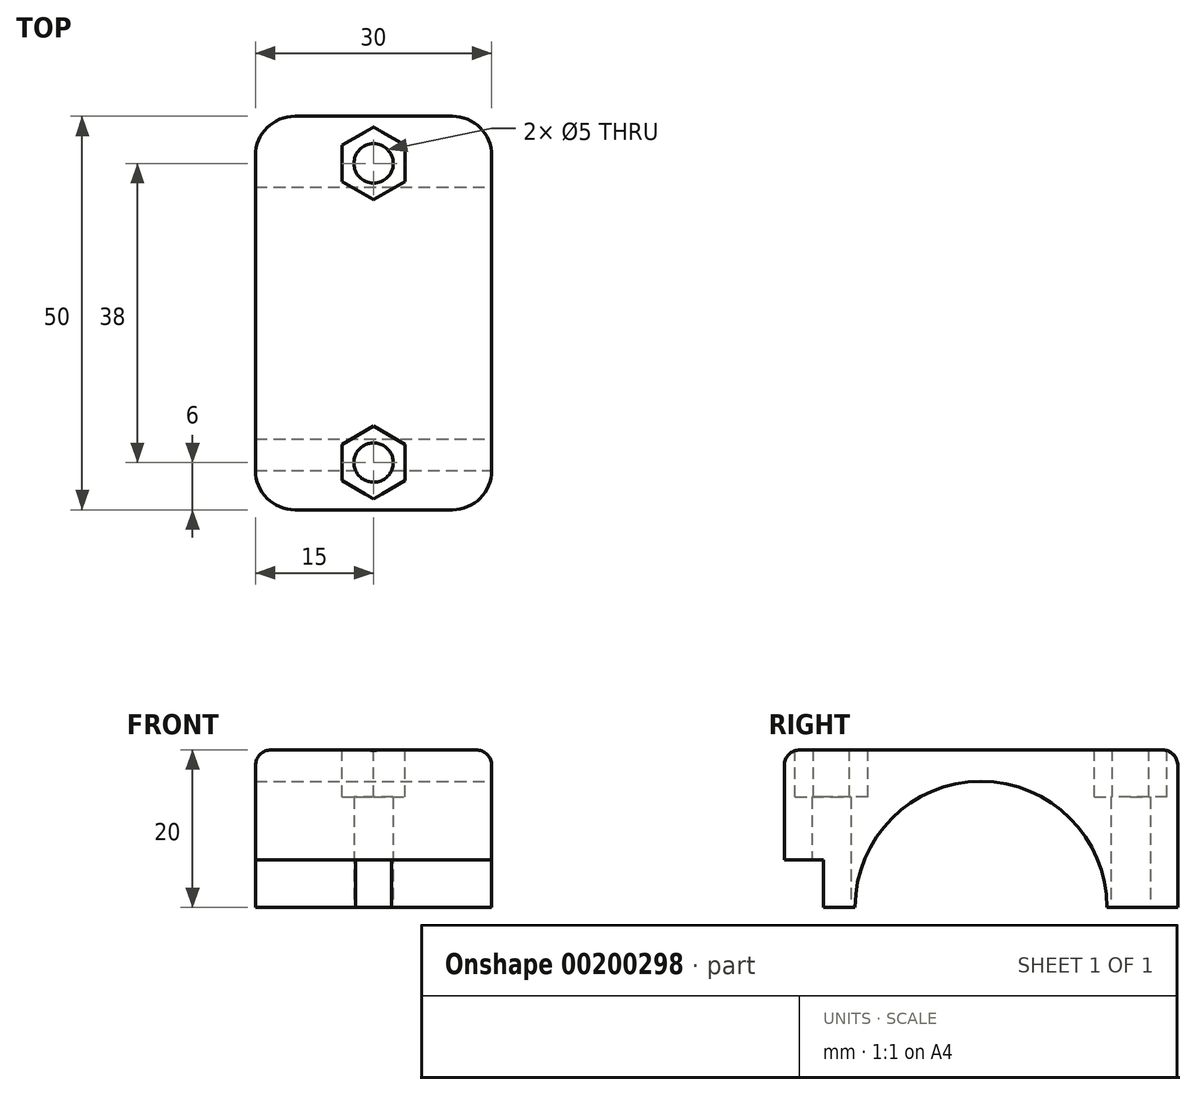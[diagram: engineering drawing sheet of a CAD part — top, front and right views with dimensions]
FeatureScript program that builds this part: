
annotation { "Feature Type Name" : "Feature", "Feature Type Description" : "" }
export const myFeature = defineFeature(function(context is Context, id is Id, definition is map)
    precondition{}
    {
        {
            var Q0;
            Q0=qCreatedBy(makeId("Top.planeOp"),FACE);
            var sketch = newSketch(context, id + "F0", { "sketchPlane" : qUnion([Q0])});
            skPoint(sketch, "E0", {"position": v(-15, 0) * mm});
            skPoint(sketch, "E1", {"position": v(15, 0) * mm});
            skPoint(sketch, "E2", {"position": v(0, 25) * mm});
            skPoint(sketch, "E3", {"position": v(0, -25) * mm});
            skPoint(sketch, "E4", {"position": v(0, 0) * mm});
            skPoint(sketch, "E5", {"position": v(0, 19) * mm});
            skPoint(sketch, "E6", {"position": v(0, -19) * mm});
            skLineSegment(sketch, "E7.bottom", {"start": v(-15, -25) * mm, "end": v(15, -25) * mm});
            skLineSegment(sketch, "E7.top", {"start": v(-15, 25) * mm, "end": v(15, 25) * mm});
            skLineSegment(sketch, "E7.left", {"start": v(-15, -25) * mm, "end": v(-15, 25) * mm});
            skLineSegment(sketch, "E7.right", {"start": v(15, -25) * mm, "end": v(15, 25) * mm});
            skLineSegment(sketch, "E8", {"start": v(-15, 0) * mm, "end": v(15, 0) * mm});
            skSolve(sketch);
        }
        {
            var Q0;
            {var subQ0=sQuery(id+"F0.wireOp",EDGE,"E7.top");Q0=makeQuery(id+"F0.imprint","IMPRINT",FACE,{"disambiguationData":[TD([[makeQuery(id+"F0.imprint","IMPRINT",EDGE,{"derivedFrom":subQ0}),-1.0]])]});}
            var Q1;
            {var subQ0=sQuery(id+"F0.wireOp",EDGE,"E7.bottom");Q1=makeQuery(id+"F0.imprint","IMPRINT",FACE,{"disambiguationData":[TD([[makeQuery(id+"F0.imprint","IMPRINT",EDGE,{"derivedFrom":subQ0}),1.0]])]});}
            extrude(context, id + "F1", {"entities" : qUnion([Q0, Q1]), "depth" : 20 * mm});
        }
        {
            var Q0;
            Q0=makeQuery(id+"F1.opExtrude","SWEPT_FACE",FACE,{"disambiguationData":[OSD([sQuery(id+"F0.wireOp",EDGE,"E7.right")])]});
            var sketch = newSketch(context, id + "F2", { "sketchPlane" : qUnion([Q0])});
            skCircle(sketch, "E9", {"center": v(0, 0) * mm, "radius": 16 * mm});
            skSolve(sketch);
        }
        {
            var Q0;
            {var subQ0=sQuery(id+"F2.wireOp",EDGE,"E9");var subQ1=makeQuery(id+"F1.opExtrude","CAP_EDGE",EDGE,{"disambiguationData":[OSD([sQuery(id+"F0.wireOp",EDGE,"E7.right")])],"isStart":true});var subQ2=makeQuery(id+"F2.imprint","INTERSECT",VERTEX,{"disambiguationData":[OD(0.0)],"derivedFrom":[subQ1,subQ0]});Q0=makeQuery(id+"F2.imprint","IMPRINT",FACE,{"disambiguationData":[TD([[makeQuery(id+"F2.imprint","IMPRINT",EDGE,{"disambiguationData":[TD([[subQ2,1.0]])],"derivedFrom":subQ0}),1.0]])]});}
            var Q1;
            {var subQ0=sQuery(id+"F2.wireOp",EDGE,"E9");var subQ1=makeQuery(id+"F1.opExtrude","CAP_EDGE",EDGE,{"disambiguationData":[OSD([sQuery(id+"F0.wireOp",EDGE,"E7.right")])],"isStart":true});var subQ2=makeQuery(id+"F2.imprint","INTERSECT",VERTEX,{"disambiguationData":[OD(0.0)],"derivedFrom":[subQ1,subQ0]});Q1=makeQuery(id+"F2.imprint","IMPRINT",FACE,{"disambiguationData":[TD([[makeQuery(id+"F2.imprint","IMPRINT",EDGE,{"disambiguationData":[TD([[subQ2,-1.0]])],"derivedFrom":subQ0}),1.0]])]});}
            extrude(context, id + "F3", {"entities" : qUnion([Q0, Q1]), "operationType" : NewBodyOperationType.REMOVE, "oppositeDirection" : true, "depth" : 50 * mm});
        }
        {
            var Q0;
            Q0=sQuery(id+"F0.wireOp",VERTEX,"E5");
            var Q1;
            Q1=sQuery(id+"F0.wireOp",VERTEX,"E6");
            var Q2;
            Q2=makeQuery(id+"F1.opExtrude","SWEPT_BODY",BODY,{"disambiguationData":[OSD([sQuery(id+"F0.wireOp",EDGE,"E7.bottom"),sQuery(id+"F0.wireOp",EDGE,"E7.top"),sQuery(id+"F0.wireOp",EDGE,"E7.left"),sQuery(id+"F0.wireOp",EDGE,"E7.right")])]});
            hole(context, id + "F4", {"style" : HoleStyle.SIMPLE, "endStyle" : HoleEndStyle.THROUGH, "oppositeDirection" : true, "holeDiameter" : 5 * mm, "locations" : qUnion([Q0, Q1]), "scope" : qUnion([Q2]), "isTappedThrough" : true});
        }
        {
            var Q0;
            Q0=makeQuery(id+"F1.opExtrude","CAP_FACE",FACE,{"disambiguationData":[OSD([sQuery(id+"F0.wireOp",EDGE,"E7.bottom"),sQuery(id+"F0.wireOp",EDGE,"E7.top"),sQuery(id+"F0.wireOp",EDGE,"E7.left"),sQuery(id+"F0.wireOp",EDGE,"E7.right")])],"isStart":false});
            var sketch = newSketch(context, id + "F5", { "sketchPlane" : qUnion([Q0])});
            skCircle(sketch, "E10.cCircle", {"center": v(0, 19) * mm, "radius": 4 * mm, "construction": true});
            skLineSegment(sketch, "E10.0", {"start": v(4, 21.3) * mm, "end": v(4, 16.7) * mm});
            skLineSegment(sketch, "E10.1", {"start": v(4, 16.7) * mm, "end": v(0, 14.38) * mm});
            skLineSegment(sketch, "E10.2", {"start": v(0, 14.38) * mm, "end": v(-4, 16.7) * mm});
            skLineSegment(sketch, "E10.3", {"start": v(-4, 16.7) * mm, "end": v(-4, 21.3) * mm});
            skLineSegment(sketch, "E10.4", {"start": v(-4, 21.3) * mm, "end": v(0, 23.62) * mm});
            skLineSegment(sketch, "E10.5", {"start": v(0, 23.62) * mm, "end": v(4, 21.3) * mm});
            skPoint(sketch, "E10.0.midPoint", {"position": v(4, 19) * mm});
            skCircle(sketch, "E11.cCircle", {"center": v(0, -19) * mm, "radius": 4 * mm, "construction": true});
            skLineSegment(sketch, "E11.0", {"start": v(4, -16.7) * mm, "end": v(4, -21.3) * mm});
            skLineSegment(sketch, "E11.1", {"start": v(4, -21.3) * mm, "end": v(0, -23.62) * mm});
            skLineSegment(sketch, "E11.2", {"start": v(0, -23.62) * mm, "end": v(-4, -21.3) * mm});
            skLineSegment(sketch, "E11.3", {"start": v(-4, -21.3) * mm, "end": v(-4, -16.7) * mm});
            skLineSegment(sketch, "E11.4", {"start": v(-4, -16.7) * mm, "end": v(0, -14.38) * mm});
            skLineSegment(sketch, "E11.5", {"start": v(0, -14.38) * mm, "end": v(4, -16.7) * mm});
            skPoint(sketch, "E11.0.midPoint", {"position": v(4, -19) * mm});
            skSolve(sketch);
        }
        {
            var Q0;
            Q0=makeQuery(id+"F5.imprint","IMPRINT",FACE,{"disambiguationData":[TD([[makeQuery(id+"F5.imprint","IMPRINT",EDGE,{"derivedFrom":sQuery(id+"F5.wireOp",EDGE,"E10.0")}),-1.0]])]});
            var Q1;
            Q1=makeQuery(id+"F5.imprint","IMPRINT",FACE,{"disambiguationData":[TD([[makeQuery(id+"F5.imprint","IMPRINT",EDGE,{"derivedFrom":sQuery(id+"F5.wireOp",EDGE,"E11.0")}),-1.0]])]});
            extrude(context, id + "F6", {"entities" : qUnion([Q0, Q1]), "operationType" : NewBodyOperationType.REMOVE, "oppositeDirection" : true, "depth" : 6 * mm});
        }
        {
            var Q0;
            Q0=makeQuery(id+"F1.opExtrude","SWEPT_EDGE",EDGE,{"disambiguationData":[OSD([sQuery(id+"F0.wireOp",EDGE,"E7.top"),sQuery(id+"F0.wireOp",EDGE,"E7.left")])]});
            var Q1;
            Q1=makeQuery(id+"F1.opExtrude","SWEPT_EDGE",EDGE,{"disambiguationData":[OSD([sQuery(id+"F0.wireOp",EDGE,"E7.top"),sQuery(id+"F0.wireOp",EDGE,"E7.right")])]});
            var Q2;
            Q2=makeQuery(id+"F1.opExtrude","SWEPT_EDGE",EDGE,{"disambiguationData":[OSD([sQuery(id+"F0.wireOp",EDGE,"E7.bottom"),sQuery(id+"F0.wireOp",EDGE,"E7.left")])]});
            var Q3;
            Q3=makeQuery(id+"F1.opExtrude","SWEPT_EDGE",EDGE,{"disambiguationData":[OSD([sQuery(id+"F0.wireOp",EDGE,"E7.bottom"),sQuery(id+"F0.wireOp",EDGE,"E7.right")])]});
            fillet(context, id + "F7", {"entities" : qUnion([Q0, Q1, Q2, Q3]), "radius" : 5 * mm, "tangentPropagation" : true, "allowEdgeOverflow" : false});
        }
        {
            var Q0;
            Q0=makeQuery(id+"F1.opExtrude","CAP_EDGE",EDGE,{"disambiguationData":[OSD([sQuery(id+"F0.wireOp",EDGE,"E7.right")])],"isStart":false});
            fillet(context, id + "F8", {"entities" : qUnion([Q0]), "radius" : 2 * mm, "tangentPropagation" : true, "allowEdgeOverflow" : false});
        }
        {
            var Q0;
            Q0=makeQuery(id+"F8.opFillet","SPLIT",FACE,{"disambiguationData":[OD(0.0)],"derivedFrom":makeQuery(id+"F1.opExtrude","SWEPT_FACE",FACE,{"disambiguationData":[OSD([sQuery(id+"F0.wireOp",EDGE,"E7.right")])]})});
            var sketch = newSketch(context, id + "F9", { "sketchPlane" : qUnion([Q0])});
            skLineSegment(sketch, "E12.bottom", {"start": v(0, 0) * mm, "end": v(-35, 0) * mm});
            skLineSegment(sketch, "E12.top", {"start": v(0, 6) * mm, "end": v(-35, 6) * mm});
            skLineSegment(sketch, "E12.left", {"start": v(0, 0) * mm, "end": v(0, 6) * mm});
            skLineSegment(sketch, "E12.right", {"start": v(-35, 0) * mm, "end": v(-35, 6) * mm});
            skSolve(sketch);
        }
        {
            var Q0;
            {var subQ4=sQuery(id+"F9.wireOp",EDGE,"E12.right");Q0=makeQuery(id+"F9.imprint","IMPRINT",FACE,{"disambiguationData":[TD([[makeQuery(id+"F9.imprint","IMPRINT",EDGE,{"derivedFrom":subQ4}),-1.0]])]});}
            var Q1;
            {var subQ3=sQuery(id+"F9.wireOp",EDGE,"E12.left");Q1=makeQuery(id+"F9.imprint","IMPRINT",FACE,{"disambiguationData":[TD([[makeQuery(id+"F9.imprint","IMPRINT",EDGE,{"derivedFrom":subQ3}),1.0]])]});}
            var Q2;
            {var subQ0=sQuery(id+"F9.wireOp",EDGE,"E12.bottom");var subQ1=makeQuery(id+"F3.boolean.opBoolean","COPY",EDGE,{"derivedFrom":makeQuery(id+"F3.opExtrude","CAP_EDGE",EDGE,{"disambiguationData":[OSD([sQuery(id+"F2.wireOp",EDGE,"E9")])],"isStart":true})});var subQ2=makeQuery(id+"F9.imprint","INTERSECT",VERTEX,{"derivedFrom":[subQ1,subQ0]});Q2=makeQuery(id+"F9.imprint","IMPRINT",FACE,{"disambiguationData":[TD([[makeQuery(id+"F9.imprint","IMPRINT",EDGE,{"disambiguationData":[TD([[subQ2,1.0]])],"derivedFrom":subQ1}),-1.0]])]});}
            extrude(context, id + "F10", {"entities" : qUnion([Q0, Q1, Q2]), "operationType" : NewBodyOperationType.REMOVE, "oppositeDirection" : true, "depth" : 50 * mm});
        }
    });
